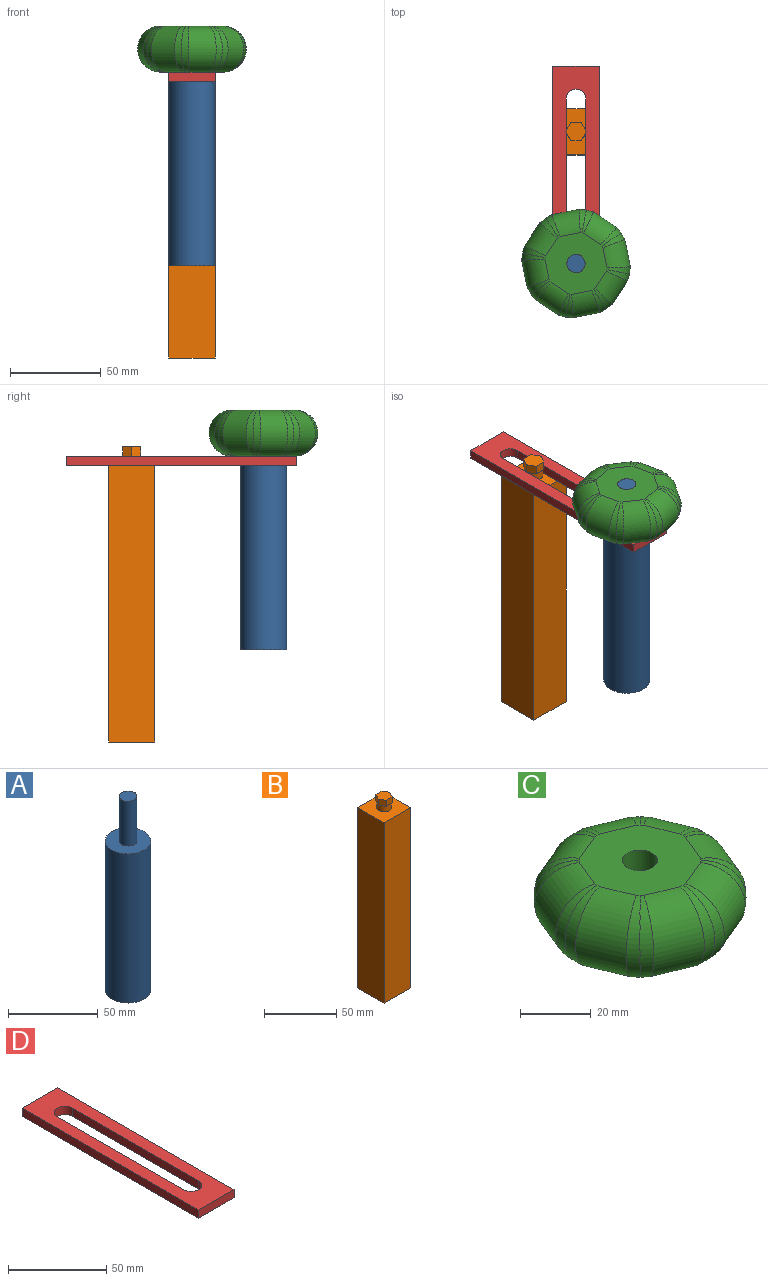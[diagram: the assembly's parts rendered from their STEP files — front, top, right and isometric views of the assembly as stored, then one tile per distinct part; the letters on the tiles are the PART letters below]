
ASSEMBLY  parts=4 mates=3
PART A: 5 faces, bbox 25.4x25.4x132.1 mm
  f0: cylinder r=12.7mm len=101.6mm, axis (0,0,-1), area 8107.3mm2, adj f1,f2
  f1: plane 25.4x25.4mm, normal (0,0,1), area 428.2mm2, adj f0,f3
  f2: plane 25.4x25.4mm, normal (0,0,-1), area 506.7mm2, adj f0
  f3: cylinder r=5mm len=30.48mm, axis (0,0,-1), area 957.6mm2, adj f1,f4
  f4: plane 10x10mm, normal (0,0,1), area 78.5mm2, adj f3
PART B: 20 faces, bbox 25.4x25.4x162.6 mm
  f0: cylinder r=5mm len=10mm, axis (0,0,-1), area 159.6mm2, adj f6,f7,f8,f9,f10,f11,f12
  f1: plane 152.4x25.4mm, normal (1,0,0), area 3871mm2, adj f2,f4,f5,f6
  f2: plane 152.4x25.4mm, normal (0,-1,0), area 3871mm2, adj f1,f3,f5,f6
  f3: plane 152.4x25.4mm, normal (-1,0,0), area 3871mm2, adj f2,f4,f5,f6
  f4: plane 152.4x25.4mm, normal (0,1,0), area 3871mm2, adj f1,f3,f5,f6
  f5: plane 25.4x25.4mm, normal (0,0,-1), area 645.2mm2, adj f1,f2,f3,f4
  f6: plane 25.4x25.4mm, normal (0,0,1), area 566.6mm2, adj f0,f1,f2,f3,f4
  f7: plane 4.33x2.5mm, normal (0,0,-1), area 1.3mm2, adj f0,f13,f18
  f8: plane 4.33x2.5mm, normal (0,0,-1), area 1.3mm2, adj f0,f13,f14
  f9: plane 5x1.44mm, normal (0,0,-1), area 1.3mm2, adj f0,f14,f15
  f10: plane 4.33x2.5mm, normal (0,0,-1), area 1.3mm2, adj f0,f15,f16
  f11: plane 4.33x2.5mm, normal (0,0,-1), area 1.3mm2, adj f0,f16,f17
  f12: plane 5x1.44mm, normal (0,0,-1), area 1.3mm2, adj f0,f17,f18
  f13: plane 5.77x5.08mm, normal (0,1,0), area 29.3mm2, adj f7,f8,f14,f18,f19
  f14: plane 5.08x5mm, normal (-0.87,0.5,0), area 29.3mm2, adj f8,f9,f13,f15,f19
  f15: plane 5.08x5mm, normal (-0.87,-0.5,0), area 29.3mm2, adj f9,f10,f14,f16,f19
  f16: plane 5.77x5.08mm, normal (0,-1,0), area 29.3mm2, adj f10,f11,f15,f17,f19
  f17: plane 5.08x5mm, normal (0.87,-0.5,0), area 29.3mm2, adj f11,f12,f16,f18,f19
  f18: plane 5.08x5mm, normal (0.87,0.5,0), area 29.3mm2, adj f7,f12,f13,f17,f19
  f19: plane 11.55x10mm, normal (0,0,1), area 86.6mm2, adj f13,f14,f15,f16,f17,f18
PART C: 27 faces, bbox 60x60x25.4 mm
  f0: plane 34.54x34.54mm, normal (0,0,1), area 797.5mm2, adj f2,f3,f4,f5,f6,f7,f8,f9
  f1: plane 34.54x34.54mm, normal (0,0,-1), area 797.5mm2, adj f2,f3,f4,f5,f6,f7,f8,f9
  f2: cylinder r=12.7mm len=25.4mm, axis (-0.07,1,0), area 115.4mm2, adj f0,f1,f3,f4
  f3: cylinder r=12.7mm len=25.4mm, axis (0.07,1,0), area 115.4mm2, adj f0,f1,f2,f5
  f4: cylinder r=12.7mm len=25.4mm, axis (-0.38,0.92,0), area 556.3mm2, adj f0,f1,f2,f6
  f5: cylinder r=12.7mm len=25.4mm, axis (0.38,0.92,0), area 556.3mm2, adj f0,f1,f3,f7
  f6: cylinder r=12.7mm len=25.4mm, axis (-0.66,0.75,0), area 115.4mm2, adj f0,f1,f4,f8
  f7: cylinder r=12.7mm len=25.4mm, axis (0.66,0.75,0), area 115.4mm2, adj f0,f1,f5,f9
  f8: cylinder r=12.7mm len=25.4mm, axis (-0.75,0.66,0), area 115.4mm2, adj f0,f1,f6,f10
  f9: cylinder r=12.7mm len=25.4mm, axis (0.75,0.66,0), area 115.4mm2, adj f0,f1,f7,f11
  f10: cylinder r=12.7mm len=25.4mm, axis (-0.92,0.38,0), area 556.3mm2, adj f0,f1,f8,f12
  f11: cylinder r=12.7mm len=25.4mm, axis (0.92,0.38,0), area 556.3mm2, adj f0,f1,f9,f13
  f12: cylinder r=12.7mm len=25.4mm, axis (-1,0.07,0), area 115.4mm2, adj f0,f1,f10,f14
  f13: cylinder r=12.7mm len=25.4mm, axis (1,0.07,0), area 115.4mm2, adj f0,f1,f11,f15
  f14: cylinder r=12.7mm len=25.4mm, axis (-1,-0.07,0), area 115.4mm2, adj f0,f1,f12,f16
  f15: cylinder r=12.7mm len=25.4mm, axis (1,-0.07,0), area 115.4mm2, adj f0,f1,f13,f17
  f16: cylinder r=12.7mm len=25.4mm, axis (-0.92,-0.38,0), area 556.3mm2, adj f0,f1,f14,f18
  f17: cylinder r=12.7mm len=25.4mm, axis (0.92,-0.38,0), area 556.3mm2, adj f0,f1,f15,f19
  f18: cylinder r=12.7mm len=25.4mm, axis (-0.75,-0.66,0), area 115.4mm2, adj f0,f1,f16,f20
  f19: cylinder r=12.7mm len=25.4mm, axis (0.75,-0.66,0), area 115.4mm2, adj f0,f1,f17,f21
  f20: cylinder r=12.7mm len=25.4mm, axis (-0.66,-0.75,0), area 115.4mm2, adj f0,f1,f18,f22
  f21: cylinder r=12.7mm len=25.4mm, axis (0.66,-0.75,0), area 115.4mm2, adj f0,f1,f19,f23
  f22: cylinder r=12.7mm len=25.4mm, axis (-0.38,-0.92,0), area 556.3mm2, adj f0,f1,f20,f24
  f23: cylinder r=12.7mm len=25.4mm, axis (0.38,-0.92,0), area 556.3mm2, adj f0,f1,f21,f25
  f24: cylinder r=12.7mm len=25.4mm, axis (-0.07,-1,0), area 115.4mm2, adj f0,f1,f22,f25
  f25: cylinder r=12.7mm len=25.4mm, axis (0.07,-1,0), area 115.4mm2, adj f0,f1,f23,f24
  f26: cylinder r=5mm len=25.4mm, axis (0,0,1), area 798mm2, adj f0,f1
PART D: 10 faces, bbox 25.4x127x5.1 mm
  f0: plane 25.4x5.08mm, normal (0,1,0), area 129mm2, adj f1,f7,f8,f9
  f1: plane 127x5.08mm, normal (-1,0,0), area 645.2mm2, adj f0,f2,f8,f9
  f2: plane 25.4x5.08mm, normal (0,-1,0), area 129mm2, adj f1,f7,f8,f9
  f3: plane 90.6x5.08mm, normal (1,0,0), area 460.2mm2, adj f4,f6,f8,f9
  f4: cylinder r=5.5mm len=11mm, axis (0,0,-1), area 87.8mm2, adj f3,f5,f8,f9
  f5: plane 90.6x5.08mm, normal (-1,0,0), area 460.2mm2, adj f4,f6,f8,f9
  f6: cylinder r=5.5mm len=11mm, axis (0,0,-1), area 87.8mm2, adj f3,f5,f8,f9
  f7: plane 127x5.08mm, normal (1,0,0), area 645.2mm2, adj f0,f2,f8,f9
  f8: plane 127x25.4mm, normal (0,0,1), area 2134.2mm2, adj f0,f1,f2,f3,f4,f5,f6,f7
  f9: plane 127x25.4mm, normal (0,0,-1), area 2134.2mm2, adj f0,f1,f2,f3,f4,f5,f6,f7
PLACE A t=(91.78,0.82,-172.72)mm fixed
PLACE B t=(-50.65,31.6,-71.12)mm
PLACE C rot(axis=(0,0,1),78.9deg) t=(-0.08,0.82,-66.04)mm
PLACE D t=(58.05,4.12,-71.12)mm
MATE slider B.f4 <-> D.f0  axis (0,1,0) through (-0.08,86.06,-71.12)mm
MATE fastened A.f0 <-> D.f6  axis (0,0,1) through (-0.08,0.82,-71.12)mm
MATE revolute A.f0 <-> C.f26  axis (0,0,-1) through (-0.08,0.82,-40.64)mm
